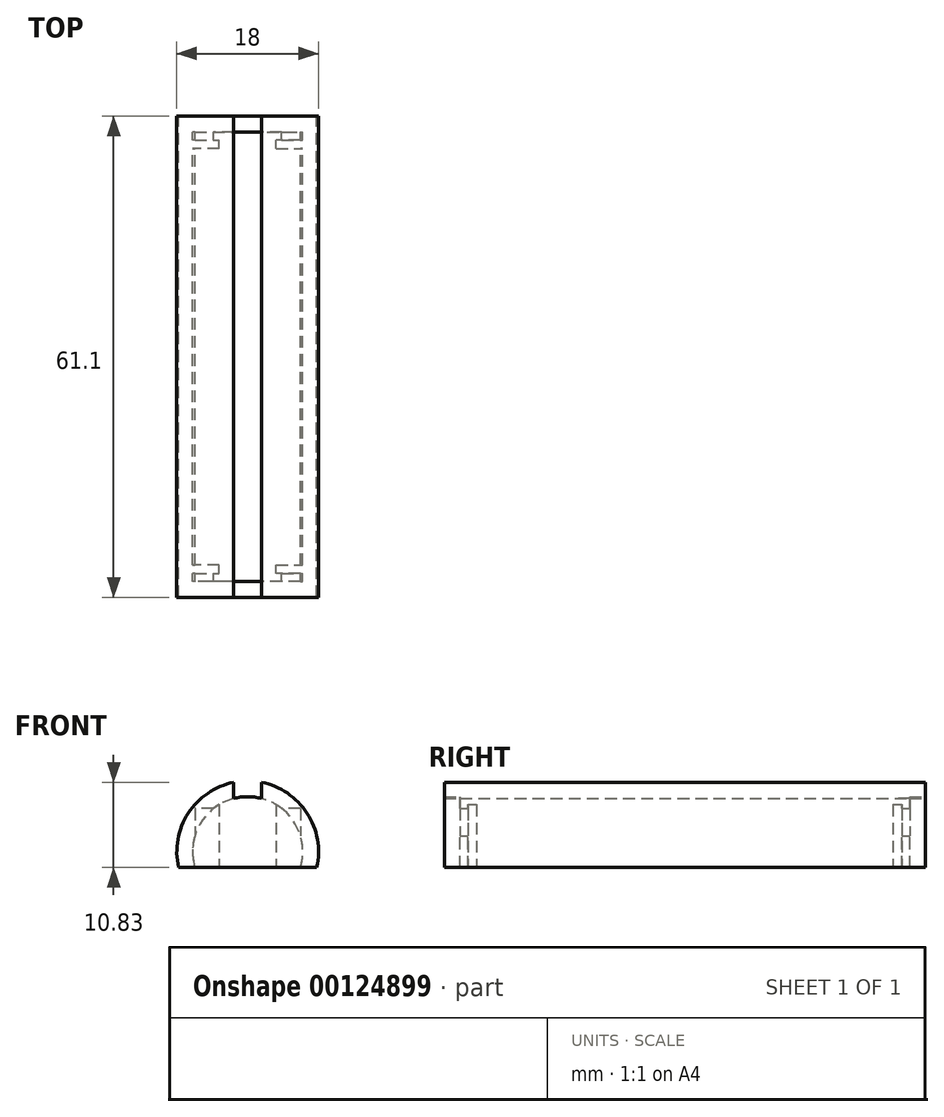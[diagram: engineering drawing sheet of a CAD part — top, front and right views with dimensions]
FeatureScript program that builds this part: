
annotation { "Feature Type Name" : "Feature", "Feature Type Description" : "" }
export const myFeature = defineFeature(function(context is Context, id is Id, definition is map)
    precondition{}
    {
        {
            assignVariable(context, id + "F0", {"name" : "battery_length", "anyValue" : 50.3 * mm});
        }
        {
            assignVariable(context, id + "F1", {"name" : "number_of_batteries", "anyValue" : 1});
        }
        {
            assignVariable(context, id + "F2", {"name" : "offset", "anyValue" : 6.8 * mm});
        }
        {
            assignVariable(context, id + "F3", {"name" : "total_length", "anyValue" : getVariable(context, 'battery_length') * getVariable(context, 'number_of_batteries') + getVariable(context, 'offset')});
        }
        {
            assignVariable(context, id + "F4", {"name" : "thickness", "anyValue" : 2 * mm});
        }
        {
            var Q0;
            Q0=qCreatedBy(makeId("Front.planeOp"),FACE);
            var sketch = newSketch(context, id + "F5", { "sketchPlane" : qUnion([Q0])});
            skArc(sketch, "E0", {"start": v(-6.7, 2) * mm, "mid": v(0, -7) * mm, "end": v(6.7, 2) * mm});
            skArc(sketch, "E1", {"start": v(-8.77, 2) * mm, "mid": v(0, -9) * mm, "end": v(8.77, 2) * mm});
            skLineSegment(sketch, "E2", {"start": v(-8.77, 2) * mm, "end": v(-6.7, 2) * mm});
            skLineSegment(sketch, "E3.trimOffspring", {"start": v(6.7, 2) * mm, "end": v(8.77, 2) * mm});
            skLineSegment(sketch, "E4", {"start": v(0, -9) * mm, "end": v(0, -3.98) * mm, "construction": true});
            skPoint(sketch, "E4.endSnap0", {"position": v(0, -7) * mm});
            skSolve(sketch);
        }
        {
            var Q0;
            Q0=makeQuery(id+"F5.imprint","IMPRINT",FACE,{"disambiguationData":[TD([[makeQuery(id+"F5.imprint","IMPRINT",EDGE,{"derivedFrom":sQuery(id+"F5.wireOp",EDGE,"E0")}),-1.0]])]});
            extrude(context, id + "F6", {"entities" : qUnion([Q0]), "depth" : getVariable(context, 'total_length')});
        }
        {
            var Q0;
            Q0=makeQuery(id+"F6.opExtrude","CAP_FACE",FACE,{"disambiguationData":[OSD([sQuery(id+"F5.wireOp",EDGE,"E0"),sQuery(id+"F5.wireOp",EDGE,"E1"),sQuery(id+"F5.wireOp",EDGE,"E2"),sQuery(id+"F5.wireOp",EDGE,"E3.trimOffspring")])],"isStart":false});
            var sketch = newSketch(context, id + "F7", { "sketchPlane" : qUnion([Q0])});
            skLineSegment(sketch, "E5", {"start": v(-6.7, 2) * mm, "end": v(6.7, 2) * mm});
            skSolve(sketch);
        }
        {
            var Q0;
            Q0=makeQuery(id+"F7.imprint","IMPRINT",FACE,{"disambiguationData":[TD([[makeQuery(id+"F7.imprint","IMPRINT",EDGE,{"derivedFrom":makeQuery(id+"F6.opExtrude","CAP_EDGE",EDGE,{"disambiguationData":[OSD([sQuery(id+"F5.wireOp",EDGE,"E0")])],"isStart":false})}),-1.0]])]});
            var Q1;
            Q1=makeQuery(id+"F7.imprint","IMPRINT",FACE,{"disambiguationData":[TD([[makeQuery(id+"F7.imprint","IMPRINT",EDGE,{"derivedFrom":sQuery(id+"F7.wireOp",EDGE,"E5")}),-1.0]])]});
            extrude(context, id + "F8", {"entities" : qUnion([Q0, Q1]), "operationType" : NewBodyOperationType.ADD, "depth" : getVariable(context, 'thickness')});
        }
        {
            var Q0;
            Q0=makeQuery(id+"F6.opExtrude","CAP_FACE",FACE,{"disambiguationData":[OSD([sQuery(id+"F5.wireOp",EDGE,"E0"),sQuery(id+"F5.wireOp",EDGE,"E1"),sQuery(id+"F5.wireOp",EDGE,"E2"),sQuery(id+"F5.wireOp",EDGE,"E3.trimOffspring")])],"isStart":true});
            var sketch = newSketch(context, id + "F9", { "sketchPlane" : qUnion([Q0])});
            skLineSegment(sketch, "E6", {"start": v(-6.7, 2) * mm, "end": v(6.7, 2) * mm});
            skSolve(sketch);
        }
        {
            var Q0;
            Q0=makeQuery(id+"F9.imprint","IMPRINT",FACE,{"disambiguationData":[TD([[makeQuery(id+"F9.imprint","IMPRINT",EDGE,{"derivedFrom":sQuery(id+"F9.wireOp",EDGE,"E6")}),-1.0]])]});
            var Q1;
            Q1=makeQuery(id+"F9.imprint","IMPRINT",FACE,{"disambiguationData":[TD([[makeQuery(id+"F9.imprint","IMPRINT",EDGE,{"derivedFrom":makeQuery(id+"F6.opExtrude","CAP_EDGE",EDGE,{"disambiguationData":[OSD([sQuery(id+"F5.wireOp",EDGE,"E0")])],"isStart":true})}),1.0]])]});
            extrude(context, id + "F10", {"entities" : qUnion([Q0, Q1]), "operationType" : NewBodyOperationType.ADD, "depth" : getVariable(context, 'thickness')});
        }
        {
            var Q0;
            {var subQ0=sQuery(id+"F5.wireOp",EDGE,"E3.trimOffspring");var subQ1=sQuery(id+"F5.wireOp",EDGE,"E2");Q0=makeQuery(id+"F10.boolean.opBoolean","MERGE",FACE,{"derivedFrom":[makeQuery(id+"F8.boolean.opBoolean","MERGE",FACE,{"derivedFrom":[makeQuery(id+"F6.opExtrude","SWEPT_FACE",FACE,{"disambiguationData":[OSD([subQ1])]}),makeQuery(id+"F6.opExtrude","SWEPT_FACE",FACE,{"disambiguationData":[OSD([subQ0])]}),makeQuery(id+"F8.opExtrude","SWEPT_FACE",FACE,{"disambiguationData":[OSD([subQ1,subQ0,sQuery(id+"F7.wireOp",EDGE,"E5")])]})]}),makeQuery(id+"F10.opExtrude","SWEPT_FACE",FACE,{"disambiguationData":[OSD([subQ1,subQ0,sQuery(id+"F9.wireOp",EDGE,"E6")])]})]});}
            var sketch = newSketch(context, id + "F11", { "sketchPlane" : qUnion([Q0])});
            skLineSegment(sketch, "E7", {"start": v(8.77, -56.1) * mm, "end": v(3.6, -56.1) * mm});
            skLineSegment(sketch, "E8", {"start": v(3.6, -56.1) * mm, "end": v(3.6, -55) * mm});
            skLineSegment(sketch, "E9", {"start": v(3.6, -55) * mm, "end": v(8.77, -55) * mm});
            skLineSegment(sketch, "E10", {"start": v(0, -57.1) * mm, "end": v(0, 0) * mm, "construction": true});
            skLineSegment(sketch, "E11", {"start": v(-6.7, -28.55) * mm, "end": v(6.7, -28.55) * mm, "construction": true});
            skLineSegment(sketch, "E12.MirrorCS", {"start": v(-3.6, -56.1) * mm, "end": v(-3.6, -55) * mm});
            skLineSegment(sketch, "E13.MirrorCS", {"start": v(-3.6, -55) * mm, "end": v(-8.77, -55) * mm});
            skLineSegment(sketch, "E14.MirrorCS", {"start": v(-8.77, -56.1) * mm, "end": v(-3.6, -56.1) * mm});
            skLineSegment(sketch, "E15.MirrorCS", {"start": v(3.6, -1) * mm, "end": v(3.6, -2.1) * mm});
            skLineSegment(sketch, "E16.MirrorCS", {"start": v(3.6, -2.1) * mm, "end": v(8.77, -2.1) * mm});
            skLineSegment(sketch, "E17.MirrorCS", {"start": v(8.77, -1) * mm, "end": v(3.6, -1) * mm});
            skLineSegment(sketch, "E18.MirrorCS", {"start": v(-3.6, -2.1) * mm, "end": v(-8.77, -2.1) * mm});
            skLineSegment(sketch, "E19.MirrorCS", {"start": v(-3.6, -1) * mm, "end": v(-3.6, -2.1) * mm});
            skLineSegment(sketch, "E20.MirrorCS", {"start": v(-8.77, -1) * mm, "end": v(-3.6, -1) * mm});
            skSolve(sketch);
        }
        {
            var Q0;
            {var subQ0=sQuery(id+"F11.wireOp",EDGE,"E12.MirrorCS");Q0=makeQuery(id+"F11.imprint","IMPRINT",FACE,{"disambiguationData":[TD([[makeQuery(id+"F11.imprint","IMPRINT",EDGE,{"derivedFrom":subQ0}),1.0]])]});}
            var Q1;
            {var subQ0=sQuery(id+"F11.wireOp",EDGE,"E14.MirrorCS");var subQ1=sQuery(id+"F5.wireOp",EDGE,"E2");var subQ5=makeQuery(id+"F6.opExtrude","SWEPT_EDGE",EDGE,{"disambiguationData":[OSD([sQuery(id+"F5.wireOp",EDGE,"E0"),subQ1])]});var subQ6=makeQuery(id+"F11.imprint","INTERSECT",VERTEX,{"derivedFrom":[subQ5,subQ0]});Q1=makeQuery(id+"F11.imprint","IMPRINT",FACE,{"disambiguationData":[TD([[makeQuery(id+"F11.imprint","IMPRINT",EDGE,{"disambiguationData":[TD([[subQ6,-1.0]])],"derivedFrom":subQ5}),1.0]])]});}
            var Q2;
            {var subQ0=sQuery(id+"F11.wireOp",EDGE,"E8");Q2=makeQuery(id+"F11.imprint","IMPRINT",FACE,{"disambiguationData":[TD([[makeQuery(id+"F11.imprint","IMPRINT",EDGE,{"derivedFrom":subQ0}),-1.0]])]});}
            var Q3;
            {var subQ0=sQuery(id+"F11.wireOp",EDGE,"E7");var subQ1=sQuery(id+"F5.wireOp",EDGE,"E3.trimOffspring");var subQ5=makeQuery(id+"F6.opExtrude","SWEPT_EDGE",EDGE,{"disambiguationData":[OSD([sQuery(id+"F5.wireOp",EDGE,"E0"),subQ1])]});var subQ6=makeQuery(id+"F11.imprint","INTERSECT",VERTEX,{"derivedFrom":[subQ5,subQ0]});Q3=makeQuery(id+"F11.imprint","IMPRINT",FACE,{"disambiguationData":[TD([[makeQuery(id+"F11.imprint","IMPRINT",EDGE,{"disambiguationData":[TD([[subQ6,-1.0]])],"derivedFrom":subQ5}),-1.0]])]});}
            var Q4;
            {var subQ0=sQuery(id+"F11.wireOp",EDGE,"E20.MirrorCS");var subQ1=sQuery(id+"F5.wireOp",EDGE,"E2");var subQ5=makeQuery(id+"F6.opExtrude","SWEPT_EDGE",EDGE,{"disambiguationData":[OSD([sQuery(id+"F5.wireOp",EDGE,"E0"),subQ1])]});var subQ6=makeQuery(id+"F11.imprint","INTERSECT",VERTEX,{"derivedFrom":[subQ5,subQ0]});Q4=makeQuery(id+"F11.imprint","IMPRINT",FACE,{"disambiguationData":[TD([[makeQuery(id+"F11.imprint","IMPRINT",EDGE,{"disambiguationData":[TD([[subQ6,1.0]])],"derivedFrom":subQ5}),1.0]])]});}
            var Q5;
            {var subQ0=sQuery(id+"F11.wireOp",EDGE,"E19.MirrorCS");Q5=makeQuery(id+"F11.imprint","IMPRINT",FACE,{"disambiguationData":[TD([[makeQuery(id+"F11.imprint","IMPRINT",EDGE,{"derivedFrom":subQ0}),-1.0]])]});}
            var Q6;
            {var subQ0=sQuery(id+"F11.wireOp",EDGE,"E17.MirrorCS");var subQ1=sQuery(id+"F5.wireOp",EDGE,"E3.trimOffspring");var subQ5=makeQuery(id+"F6.opExtrude","SWEPT_EDGE",EDGE,{"disambiguationData":[OSD([sQuery(id+"F5.wireOp",EDGE,"E0"),subQ1])]});var subQ6=makeQuery(id+"F11.imprint","INTERSECT",VERTEX,{"derivedFrom":[subQ5,subQ0]});Q6=makeQuery(id+"F11.imprint","IMPRINT",FACE,{"disambiguationData":[TD([[makeQuery(id+"F11.imprint","IMPRINT",EDGE,{"disambiguationData":[TD([[subQ6,1.0]])],"derivedFrom":subQ5}),-1.0]])]});}
            var Q7;
            {var subQ0=sQuery(id+"F11.wireOp",EDGE,"E15.MirrorCS");Q7=makeQuery(id+"F11.imprint","IMPRINT",FACE,{"disambiguationData":[TD([[makeQuery(id+"F11.imprint","IMPRINT",EDGE,{"derivedFrom":subQ0}),1.0]])]});}
            var Q8;
            Q8=makeQuery(id+"F6.opExtrude","SWEPT_BODY",BODY,{"disambiguationData":[OSD([sQuery(id+"F5.wireOp",EDGE,"E0"),sQuery(id+"F5.wireOp",EDGE,"E1"),sQuery(id+"F5.wireOp",EDGE,"E2"),sQuery(id+"F5.wireOp",EDGE,"E3.trimOffspring")])]});
            extrude(context, id + "F12", {"entities" : qUnion([Q0, Q1, Q2, Q3, Q4, Q5, Q6, Q7]), "operationType" : NewBodyOperationType.ADD, "endBound" : BoundingType.UP_TO_BODY, "oppositeDirection" : true, "endBoundEntityBody" : qUnion([Q8]), "depth" : 25 * mm});
        }
        {
            var Q0;
            {var subQ0=sQuery(id+"F5.wireOp",EDGE,"E2");var subQ1=sQuery(id+"F5.wireOp",EDGE,"E1");var subQ2=sQuery(id+"F5.wireOp",EDGE,"E3.trimOffspring");Q0=makeQuery(id+"F12.boolean.opBoolean","MERGE",FACE,{"derivedFrom":[makeQuery(id+"F10.boolean.opBoolean","MERGE",FACE,{"derivedFrom":[makeQuery(id+"F8.boolean.opBoolean","MERGE",FACE,{"derivedFrom":[makeQuery(id+"F6.opExtrude","SWEPT_FACE",FACE,{"disambiguationData":[OSD([subQ0])]}),makeQuery(id+"F6.opExtrude","SWEPT_FACE",FACE,{"disambiguationData":[OSD([subQ2])]}),makeQuery(id+"F8.opExtrude","SWEPT_FACE",FACE,{"disambiguationData":[OSD([subQ0,subQ2,sQuery(id+"F7.wireOp",EDGE,"E5")])]})]}),makeQuery(id+"F10.opExtrude","SWEPT_FACE",FACE,{"disambiguationData":[OSD([subQ0,subQ2,sQuery(id+"F9.wireOp",EDGE,"E6")])]})]}),makeQuery(id+"F12.opExtrude","CAP_FACE",FACE,{"disambiguationData":[OSD([subQ1,subQ0,sQuery(id+"F11.wireOp",EDGE,"E12.MirrorCS"),sQuery(id+"F11.wireOp",EDGE,"E14.MirrorCS"),sQuery(id+"F11.wireOp",EDGE,"E13.MirrorCS")])],"isStart":true}),makeQuery(id+"F12.opExtrude","CAP_FACE",FACE,{"disambiguationData":[OSD([subQ1,subQ2,sQuery(id+"F11.wireOp",EDGE,"E7"),sQuery(id+"F11.wireOp",EDGE,"E9"),sQuery(id+"F11.wireOp",EDGE,"E8")])],"isStart":true}),makeQuery(id+"F12.opExtrude","CAP_FACE",FACE,{"disambiguationData":[OSD([subQ1,subQ2,sQuery(id+"F11.wireOp",EDGE,"E15.MirrorCS"),sQuery(id+"F11.wireOp",EDGE,"E17.MirrorCS"),sQuery(id+"F11.wireOp",EDGE,"E16.MirrorCS")])],"isStart":true}),makeQuery(id+"F12.opExtrude","CAP_FACE",FACE,{"disambiguationData":[OSD([subQ1,subQ0,sQuery(id+"F11.wireOp",EDGE,"E19.MirrorCS"),sQuery(id+"F11.wireOp",EDGE,"E20.MirrorCS"),sQuery(id+"F11.wireOp",EDGE,"E18.MirrorCS")])],"isStart":true})]});}
            var sketch = newSketch(context, id + "F13", { "sketchPlane" : qUnion([Q0])});
            skLineSegment(sketch, "E21", {"start": v(-1.75, -57.1) * mm, "end": v(-1.75, -55.7) * mm});
            skLineSegment(sketch, "E22", {"start": v(-1.75, -55.7) * mm, "end": v(0, -55.7) * mm});
            skLineSegment(sketch, "E23", {"start": v(1.75, -55.7) * mm, "end": v(1.75, -57.1) * mm});
            skLineSegment(sketch, "E24", {"start": v(0, -57.1) * mm, "end": v(0, -54.22) * mm, "construction": true});
            skLineSegment(sketch, "E25", {"start": v(0, -55.7) * mm, "end": v(1.75, -55.7) * mm});
            skLineSegment(sketch, "E26", {"start": v(-6.7, -28.55) * mm, "end": v(6.7, -28.55) * mm, "construction": true});
            skLineSegment(sketch, "E27.MirrorCS", {"start": v(1.75, -55.7) * mm, "end": v(0, -55.7) * mm});
            skLineSegment(sketch, "E28.MirrorCS", {"start": v(1.75, -57.1) * mm, "end": v(1.75, -55.7) * mm});
            skLineSegment(sketch, "E29.MirrorCS", {"start": v(-1.75, -55.7) * mm, "end": v(-1.75, -57.1) * mm});
            skLineSegment(sketch, "E30.MirrorCS", {"start": v(0, -55.7) * mm, "end": v(-1.75, -55.7) * mm});
            skLineSegment(sketch, "E31.MirrorCS", {"start": v(6.7, -28.55) * mm, "end": v(-6.7, -28.55) * mm, "construction": true});
            skLineSegment(sketch, "E32.MirrorCS", {"start": v(1.75, 0) * mm, "end": v(1.75, -1.4) * mm});
            skLineSegment(sketch, "E33.MirrorCS", {"start": v(1.75, -1.4) * mm, "end": v(0, -1.4) * mm});
            skLineSegment(sketch, "E34.MirrorCS", {"start": v(-1.75, -1.4) * mm, "end": v(-1.75, 0) * mm});
            skLineSegment(sketch, "E35.MirrorCS", {"start": v(0, -1.4) * mm, "end": v(-1.75, -1.4) * mm});
            skSolve(sketch);
        }
        {
            var Q0;
            Q0=makeQuery(id+"F13.imprint","IMPRINT",FACE,{"disambiguationData":[TD([[makeQuery(id+"F13.imprint","IMPRINT",EDGE,{"derivedFrom":sQuery(id+"F13.wireOp",EDGE,"E27.MirrorCS")}),1.0]])]});
            var Q1;
            {var subQ1=sQuery(id+"F13.wireOp",EDGE,"E32.MirrorCS");Q1=makeQuery(id+"F13.imprint","IMPRINT",FACE,{"disambiguationData":[TD([[makeQuery(id+"F13.imprint","IMPRINT",EDGE,{"derivedFrom":subQ1}),-1.0]])]});}
            extrude(context, id + "F14", {"entities" : qUnion([Q0, Q1]), "operationType" : NewBodyOperationType.REMOVE, "endBound" : BoundingType.THROUGH_ALL, "oppositeDirection" : true, "depth" : 25 * mm});
        }
        {
            var Q0;
            {var subQ0=sQuery(id+"F5.wireOp",EDGE,"E2");var subQ1=sQuery(id+"F5.wireOp",EDGE,"E1");var subQ2=sQuery(id+"F5.wireOp",EDGE,"E3.trimOffspring");Q0=makeQuery(id+"F12.boolean.opBoolean","MERGE",FACE,{"derivedFrom":[makeQuery(id+"F10.boolean.opBoolean","MERGE",FACE,{"derivedFrom":[makeQuery(id+"F8.boolean.opBoolean","MERGE",FACE,{"derivedFrom":[makeQuery(id+"F6.opExtrude","SWEPT_FACE",FACE,{"disambiguationData":[OSD([subQ0])]}),makeQuery(id+"F6.opExtrude","SWEPT_FACE",FACE,{"disambiguationData":[OSD([subQ2])]}),makeQuery(id+"F8.opExtrude","SWEPT_FACE",FACE,{"disambiguationData":[OSD([subQ0,subQ2,sQuery(id+"F7.wireOp",EDGE,"E5")])]})]}),makeQuery(id+"F10.opExtrude","SWEPT_FACE",FACE,{"disambiguationData":[OSD([subQ0,subQ2,sQuery(id+"F9.wireOp",EDGE,"E6")])]})]}),makeQuery(id+"F12.opExtrude","CAP_FACE",FACE,{"disambiguationData":[OSD([subQ1,subQ0,sQuery(id+"F11.wireOp",EDGE,"E12.MirrorCS"),sQuery(id+"F11.wireOp",EDGE,"E14.MirrorCS"),sQuery(id+"F11.wireOp",EDGE,"E13.MirrorCS")])],"isStart":true}),makeQuery(id+"F12.opExtrude","CAP_FACE",FACE,{"disambiguationData":[OSD([subQ1,subQ2,sQuery(id+"F11.wireOp",EDGE,"E7"),sQuery(id+"F11.wireOp",EDGE,"E9"),sQuery(id+"F11.wireOp",EDGE,"E8")])],"isStart":true}),makeQuery(id+"F12.opExtrude","CAP_FACE",FACE,{"disambiguationData":[OSD([subQ1,subQ2,sQuery(id+"F11.wireOp",EDGE,"E15.MirrorCS"),sQuery(id+"F11.wireOp",EDGE,"E17.MirrorCS"),sQuery(id+"F11.wireOp",EDGE,"E16.MirrorCS")])],"isStart":true}),makeQuery(id+"F12.opExtrude","CAP_FACE",FACE,{"disambiguationData":[OSD([subQ1,subQ0,sQuery(id+"F11.wireOp",EDGE,"E19.MirrorCS"),sQuery(id+"F11.wireOp",EDGE,"E20.MirrorCS"),sQuery(id+"F11.wireOp",EDGE,"E18.MirrorCS")])],"isStart":true})]});}
            var sketch = newSketch(context, id + "F15", { "sketchPlane" : qUnion([Q0])});
            skLineSegment(sketch, "E36.bottom", {"start": v(6.7, 0) * mm, "end": v(-6.7, 0) * mm});
            skLineSegment(sketch, "E36.top", {"start": v(6.7, -1) * mm, "end": v(-6.7, -1) * mm});
            skLineSegment(sketch, "E36.left", {"start": v(6.7, 0) * mm, "end": v(6.7, -1) * mm});
            skLineSegment(sketch, "E36.right", {"start": v(-6.7, 0) * mm, "end": v(-6.7, -1) * mm});
            skLineSegment(sketch, "E37.bottom", {"start": v(6.7, -57.1) * mm, "end": v(-6.7, -57.1) * mm});
            skLineSegment(sketch, "E37.top", {"start": v(6.7, -56.1) * mm, "end": v(-6.7, -56.1) * mm});
            skLineSegment(sketch, "E37.left", {"start": v(6.7, -57.1) * mm, "end": v(6.7, -56.1) * mm});
            skLineSegment(sketch, "E37.right", {"start": v(-6.7, -57.1) * mm, "end": v(-6.7, -56.1) * mm});
            skSolve(sketch);
        }
        {
            var Q0;
            Q0=makeQuery(id+"F15.imprint","IMPRINT",FACE,{"disambiguationData":[TD([[makeQuery(id+"F15.imprint","IMPRINT",EDGE,{"derivedFrom":sQuery(id+"F15.wireOp",EDGE,"E37.bottom")}),1.0]])]});
            var Q1;
            Q1=makeQuery(id+"F15.imprint","IMPRINT",FACE,{"disambiguationData":[TD([[makeQuery(id+"F15.imprint","IMPRINT",EDGE,{"derivedFrom":sQuery(id+"F15.wireOp",EDGE,"E36.bottom")}),1.0]])]});
            var Q2;
            Q2=makeQuery(id+"F6.opExtrude","SWEPT_FACE",FACE,{"disambiguationData":[OSD([sQuery(id+"F5.wireOp",EDGE,"E0")])]});
            extrude(context, id + "F16", {"entities" : qUnion([Q0, Q1]), "operationType" : NewBodyOperationType.REMOVE, "oppositeDirection" : true, "endBoundEntityFace" : qUnion([Q2]), "depth" : 7.5 * mm});
        }
        {
            var Q0;
            Q0=sQuery(id+"F5.wireOp",VERTEX,"E4.start");
            var Q1;
            {var subQ0=sQuery(id+"F5.wireOp",EDGE,"E2");var subQ1=sQuery(id+"F5.wireOp",EDGE,"E1");var subQ2=sQuery(id+"F5.wireOp",EDGE,"E3.trimOffspring");Q1=makeQuery(id+"F12.boolean.opBoolean","MERGE",FACE,{"derivedFrom":[makeQuery(id+"F10.boolean.opBoolean","MERGE",FACE,{"derivedFrom":[makeQuery(id+"F8.boolean.opBoolean","MERGE",FACE,{"derivedFrom":[makeQuery(id+"F6.opExtrude","SWEPT_FACE",FACE,{"disambiguationData":[OSD([subQ0])]}),makeQuery(id+"F6.opExtrude","SWEPT_FACE",FACE,{"disambiguationData":[OSD([subQ2])]}),makeQuery(id+"F8.opExtrude","SWEPT_FACE",FACE,{"disambiguationData":[OSD([subQ0,subQ2,sQuery(id+"F7.wireOp",EDGE,"E5")])]})]}),makeQuery(id+"F10.opExtrude","SWEPT_FACE",FACE,{"disambiguationData":[OSD([subQ0,subQ2,sQuery(id+"F9.wireOp",EDGE,"E6")])]})]}),makeQuery(id+"F12.opExtrude","CAP_FACE",FACE,{"disambiguationData":[OSD([subQ1,subQ0,sQuery(id+"F11.wireOp",EDGE,"E12.MirrorCS"),sQuery(id+"F11.wireOp",EDGE,"E14.MirrorCS"),sQuery(id+"F11.wireOp",EDGE,"E13.MirrorCS")])],"isStart":true}),makeQuery(id+"F12.opExtrude","CAP_FACE",FACE,{"disambiguationData":[OSD([subQ1,subQ2,sQuery(id+"F11.wireOp",EDGE,"E7"),sQuery(id+"F11.wireOp",EDGE,"E9"),sQuery(id+"F11.wireOp",EDGE,"E8")])],"isStart":true}),makeQuery(id+"F12.opExtrude","CAP_FACE",FACE,{"disambiguationData":[OSD([subQ1,subQ2,sQuery(id+"F11.wireOp",EDGE,"E15.MirrorCS"),sQuery(id+"F11.wireOp",EDGE,"E17.MirrorCS"),sQuery(id+"F11.wireOp",EDGE,"E16.MirrorCS")])],"isStart":true}),makeQuery(id+"F12.opExtrude","CAP_FACE",FACE,{"disambiguationData":[OSD([subQ1,subQ0,sQuery(id+"F11.wireOp",EDGE,"E19.MirrorCS"),sQuery(id+"F11.wireOp",EDGE,"E20.MirrorCS"),sQuery(id+"F11.wireOp",EDGE,"E18.MirrorCS")])],"isStart":true})]});}
            cPlane(context, id + "F17", {"entities" : qUnion([Q0, Q1]), "cplaneType" : CPlaneType.PLANE_POINT, "offset" : 25 * mm, "width" : 150 * mm, "height" : 150 * mm});
        }
        {
            var Q0;
            Q0=qCreatedBy(id+"F17.planeOp",FACE);
            var sketch = newSketch(context, id + "F18", { "sketchPlane" : qUnion([Q0])});
            skLineSegment(sketch, "E38", {"start": v(-1.75, 2.09) * mm, "end": v(-1.75, -59.13) * mm});
            skLineSegment(sketch, "E39", {"start": v(-1.75, -59.13) * mm, "end": v(1.76, -59.13) * mm});
            skLineSegment(sketch, "E40", {"start": v(1.76, -59.13) * mm, "end": v(1.76, 2.09) * mm});
            skLineSegment(sketch, "E41", {"start": v(1.76, 2.09) * mm, "end": v(-1.75, 2.09) * mm});
            skSolve(sketch);
        }
        {
            var Q0;
            Q0=makeQuery(id+"F18.imprint","IMPRINT",FACE,{"disambiguationData":[TD([[makeQuery(id+"F18.imprint","IMPRINT",EDGE,{"derivedFrom":sQuery(id+"F18.wireOp",EDGE,"E38")}),1.0]])]});
            var Q1;
            {var subQ15=sQuery(id+"F11.wireOp",EDGE,"E12.MirrorCS");Q1=makeQuery(id+"F16.boolean.opBoolean","SPLIT",FACE,{"disambiguationData":[TD([makeQuery(id+"F12.opExtrude","SWEPT_FACE",FACE,{"disambiguationData":[OSD([subQ15])]})])],"derivedFrom":makeQuery(id+"F6.opExtrude","SWEPT_FACE",FACE,{"disambiguationData":[OSD([sQuery(id+"F5.wireOp",EDGE,"E0")])]})});}
            extrude(context, id + "F19", {"entities" : qUnion([Q0]), "operationType" : NewBodyOperationType.REMOVE, "endBound" : BoundingType.UP_TO_SURFACE, "endBoundEntityFace" : qUnion([Q1]), "depth" : 4 * mm});
        }
        {
            var Q0;
            Q0=makeQuery(id+"F6.opExtrude","SWEPT_BODY",BODY,{"disambiguationData":[OSD([sQuery(id+"F5.wireOp",EDGE,"E0"),sQuery(id+"F5.wireOp",EDGE,"E1"),sQuery(id+"F5.wireOp",EDGE,"E2"),sQuery(id+"F5.wireOp",EDGE,"E3.trimOffspring")])]});
            var Q1;
            {var subQ0=sQuery(id+"F11.wireOp",EDGE,"E13.MirrorCS");var subQ4=sQuery(id+"F5.wireOp",EDGE,"E2");var subQ5=sQuery(id+"F5.wireOp",EDGE,"E0");Q1=makeQuery(id+"F12.boolean.opBoolean","SPLIT",EDGE,{"disambiguationData":[TD([makeQuery(id+"F12.opExtrude","SWEPT_FACE",FACE,{"disambiguationData":[OSD([subQ0])]})])],"derivedFrom":makeQuery(id+"F6.opExtrude","SWEPT_EDGE",EDGE,{"disambiguationData":[OSD([subQ5,subQ4])]})});}
            transform(context, id + "F20", {"entities" : qUnion([Q0]), "transformType" : TransformType.ROTATION, "transformAxis" : qUnion([Q1]), "angle" : 180 * degree, "makeCopy" : false});
        }
    });
